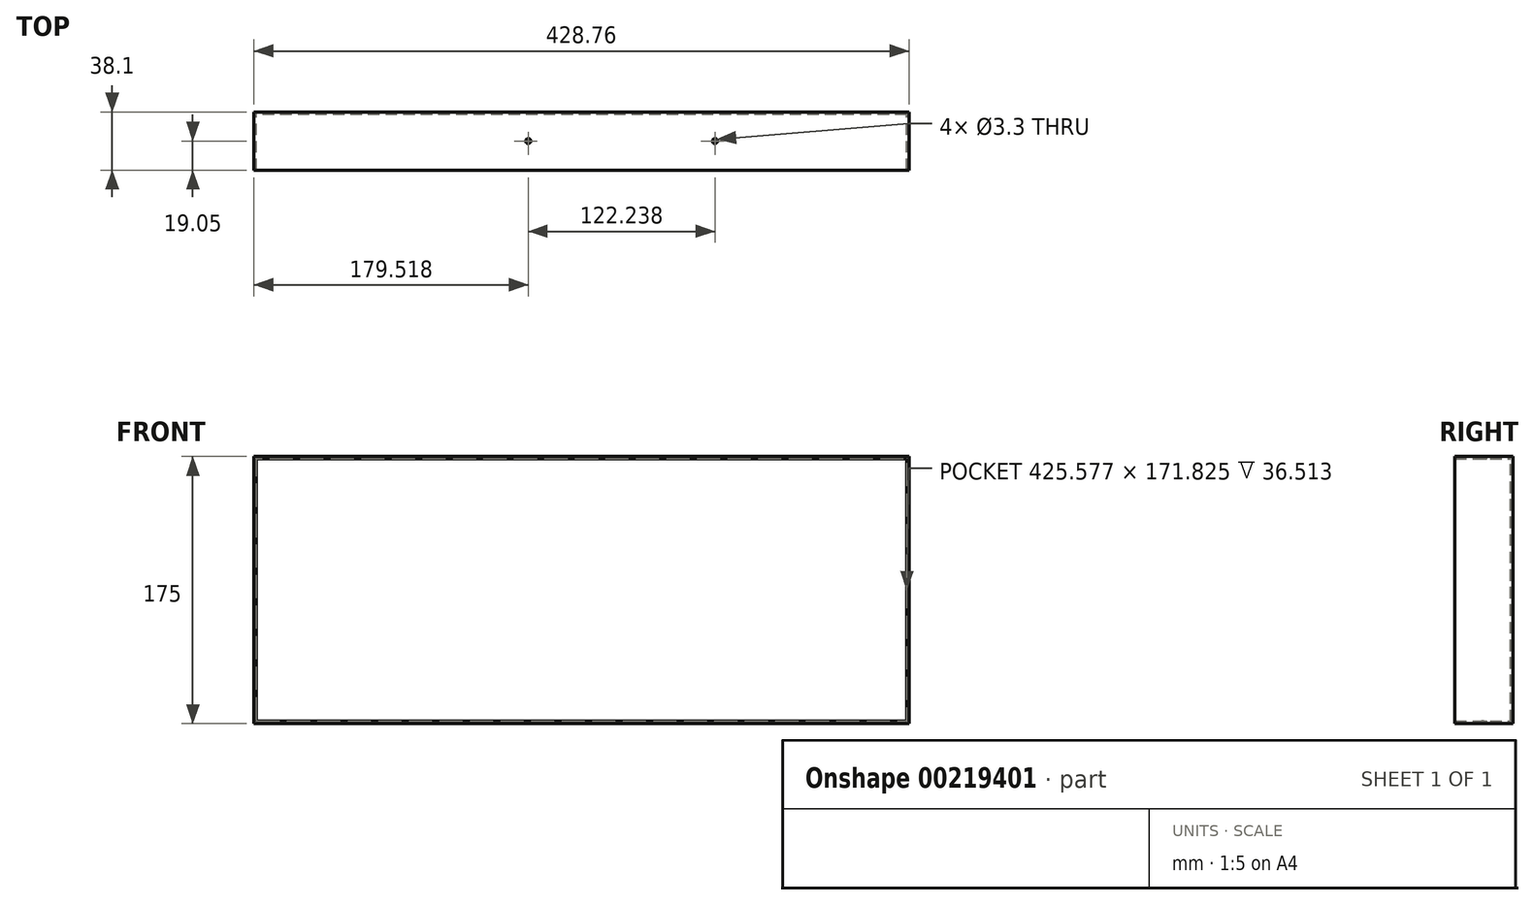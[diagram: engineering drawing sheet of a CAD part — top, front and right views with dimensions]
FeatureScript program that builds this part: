
annotation { "Feature Type Name" : "Feature", "Feature Type Description" : "" }
export const myFeature = defineFeature(function(context is Context, id is Id, definition is map)
    precondition{}
    {
        {
            var Q0;
            Q0=qCreatedBy(makeId("Front.planeOp"),FACE);
            var sketch = newSketch(context, id + "F0", { "sketchPlane" : qUnion([Q0])});
            skLineSegment(sketch, "E0.bottom", {"start": v(214.38, -87.5) * mm, "end": v(-214.38, -87.5) * mm});
            skLineSegment(sketch, "E0.top", {"start": v(214.38, 87.5) * mm, "end": v(-214.38, 87.5) * mm});
            skLineSegment(sketch, "E0.left", {"start": v(214.38, -87.5) * mm, "end": v(214.38, 87.5) * mm});
            skLineSegment(sketch, "E0.right", {"start": v(-214.38, -87.5) * mm, "end": v(-214.38, 87.5) * mm});
            skPoint(sketch, "E0.middle", {"position": v(0, 0) * mm});
            skSolve(sketch);
        }
        {
            var Q0;
            Q0 = qSketchRegion(id + "F0", true);
            extrude(context, id + "F1", {"entities" : qUnion([Q0]), "depth" : 38.1 * mm, "offsetDistance" : 25.4 * mm});
        }
        {
            var Q0;
            Q0=makeQuery(id+"F1.opExtrude","CAP_FACE",FACE,{"disambiguationData":[OSD([sQuery(id+"F0.wireOp",EDGE,"E0.bottom"),sQuery(id+"F0.wireOp",EDGE,"E0.top"),sQuery(id+"F0.wireOp",EDGE,"E0.left"),sQuery(id+"F0.wireOp",EDGE,"E0.right")])],"isStart":false});
            shell(context, id + "F2", {"entities" : qUnion([Q0]), "thickness" : 1.59 * mm});
        }
        {
            var Q0;
            Q0=makeQuery(id+"F1.opExtrude","SWEPT_FACE",FACE,{"disambiguationData":[OSD([sQuery(id+"F0.wireOp",EDGE,"E0.bottom")])]});
            var sketch = newSketch(context, id + "F3", { "sketchPlane" : qUnion([Q0])});
            skPoint(sketch, "E1", {"position": v(87.38, 19.05) * mm});
            skPoint(sketch, "E1.positionSnap0", {"position": v(214.38, 19.05) * mm});
            skPoint(sketch, "E2", {"position": v(-34.86, 19.05) * mm});
            skSolve(sketch);
        }
        {
            var Q0;
            Q0=sQuery(id+"F3.wireOp",VERTEX,"E2");
            var Q1;
            Q1=sQuery(id+"F3.wireOp",VERTEX,"E1");
            var Q2;
            Q2=makeQuery(id+"F1.opExtrude","SWEPT_BODY",BODY,{"disambiguationData":[OSD([sQuery(id+"F0.wireOp",EDGE,"E0.bottom"),sQuery(id+"F0.wireOp",EDGE,"E0.top"),sQuery(id+"F0.wireOp",EDGE,"E0.left"),sQuery(id+"F0.wireOp",EDGE,"E0.right")])]});
            hole(context, id + "F4", {"style" : HoleStyle.SIMPLE, "endStyle" : HoleEndStyle.THROUGH, "standardTappedOrClearance" : lookupTablePath({ "standard" : "ISO", "fit" : "Normal", "size" : "M3", "type" : "Clearance" }), "standardBlindInLast" : lookupTablePath({ "fit" : "Standard", "standard" : "ISO", "size" : "M3", "type" : "Clearance" }), "holeDiameter" : 3.3 * mm, "majorDiameter" : 6.35 * mm, "tappedDepth" : 12.7 * mm, "tapClearance" : 3, "locations" : qUnion([Q0, Q1]), "scope" : qUnion([Q2]), "startStyle" : HoleStartStyle.SKETCH});
        }
    });
